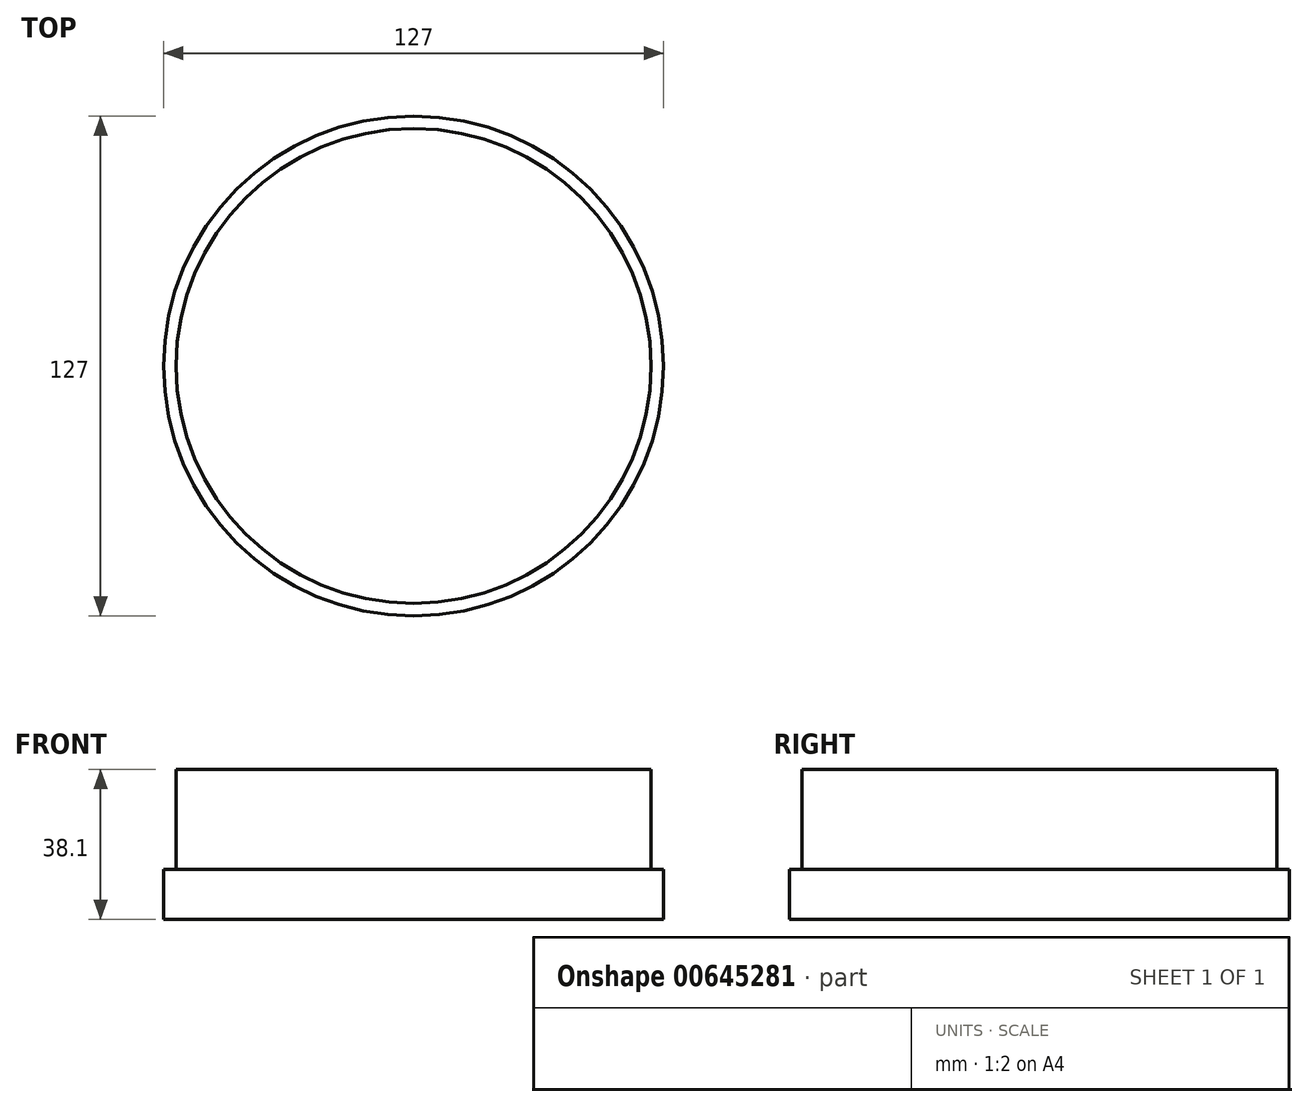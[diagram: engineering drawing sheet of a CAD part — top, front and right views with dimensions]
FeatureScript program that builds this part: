
annotation { "Feature Type Name" : "Feature", "Feature Type Description" : "" }
export const myFeature = defineFeature(function(context is Context, id is Id, definition is map)
    precondition{}
    {
        {
            var Q0;
            Q0=qCreatedBy(makeId("Top.planeOp"),FACE);
            var sketch = newSketch(context, id + "F0", { "sketchPlane" : qUnion([Q0])});
            skCircle(sketch, "E0", {"center": v(0, 0) * mm, "radius": 63.5 * mm});
            skSolve(sketch);
        }
        {
            var Q0;
            Q0=makeQuery(id+"F0.imprint","IMPRINT",FACE,{"disambiguationData":[TD([[makeQuery(id+"F0.imprint","IMPRINT",EDGE,{"derivedFrom":sQuery(id+"F0.wireOp",EDGE,"E0")}),1.0]])]});
            extrude(context, id + "F1", {"entities" : qUnion([Q0]), "oppositeDirection" : true, "depth" : 12.7 * mm, "offsetDistance" : 25.4 * mm});
        }
        {
            var Q0;
            Q0=qCreatedBy(makeId("Top.planeOp"),FACE);
            var sketch = newSketch(context, id + "F2", { "sketchPlane" : qUnion([Q0])});
            skCircle(sketch, "E1", {"center": v(0, 0) * mm, "radius": 60.33 * mm});
            skSolve(sketch);
        }
        {
            var Q0;
            Q0=makeQuery(id+"F2.imprint","IMPRINT",FACE,{"disambiguationData":[TD([[makeQuery(id+"F2.imprint","IMPRINT",EDGE,{"derivedFrom":sQuery(id+"F2.wireOp",EDGE,"E1")}),1.0]])]});
            var Q1;
            Q1=sQuery(id+"F2.wireOp",EDGE,"E1");
            extrude(context, id + "F3", {"entities" : qUnion([Q0]), "operationType" : NewBodyOperationType.ADD, "surfaceEntities" : qUnion([Q1]), "depth" : 25.4 * mm, "offsetDistance" : 25.4 * mm});
        }
    });
